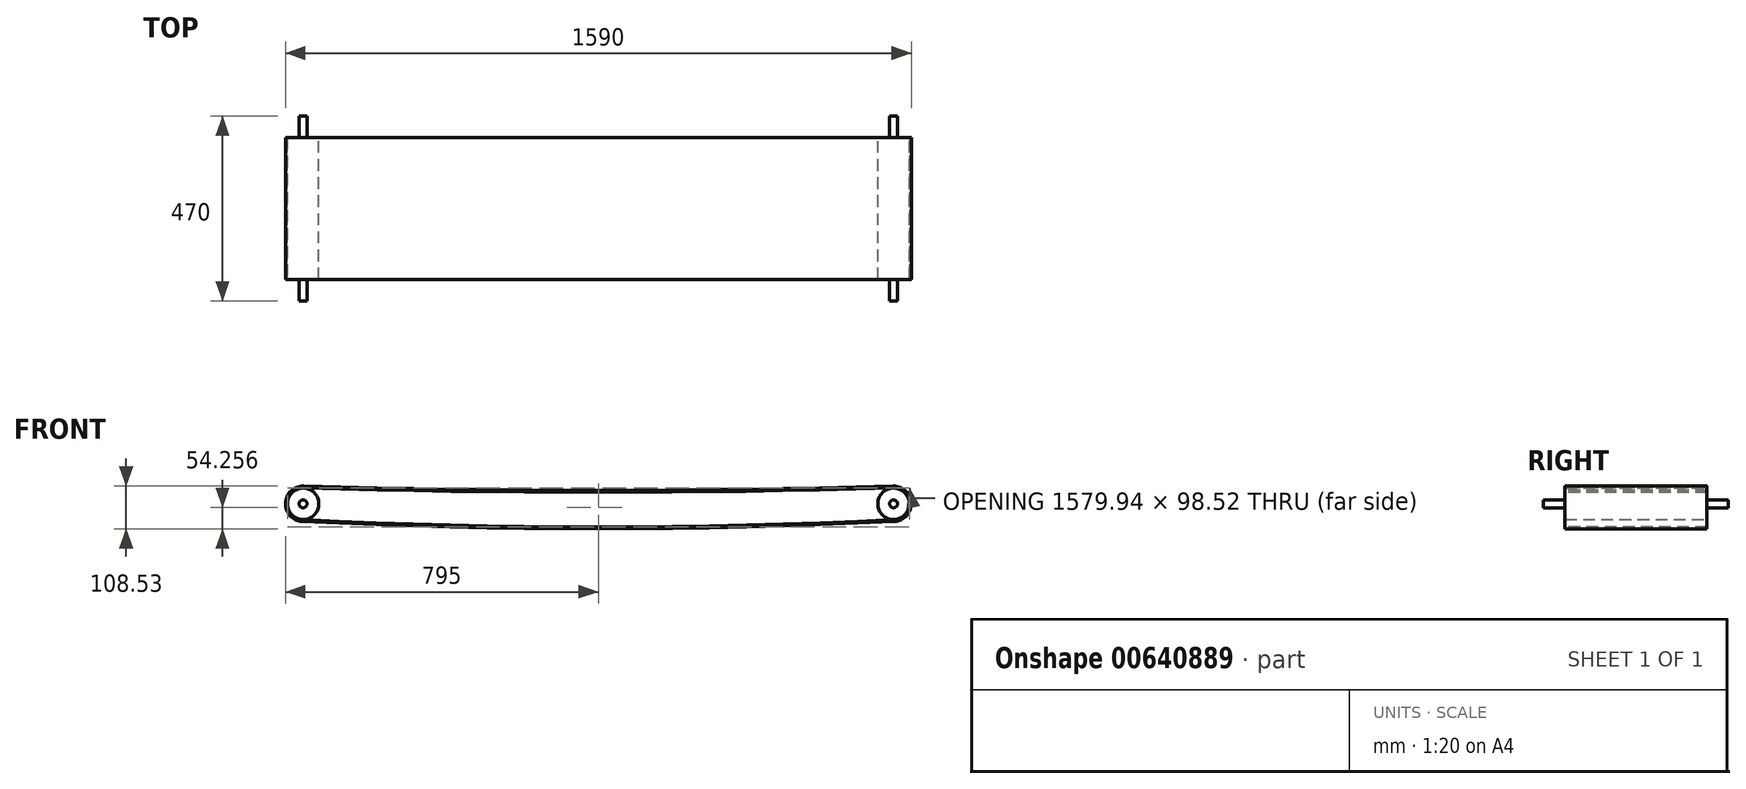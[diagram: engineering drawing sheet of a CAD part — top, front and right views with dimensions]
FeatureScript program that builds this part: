
annotation { "Feature Type Name" : "Feature", "Feature Type Description" : "" }
export const myFeature = defineFeature(function(context is Context, id is Id, definition is map)
    precondition{}
    {
        {
            var Q0;
            Q0=qCreatedBy(makeId("Front.planeOp"),FACE);
            var sketch = newSketch(context, id + "F0", { "sketchPlane" : qUnion([Q0])});
            skCircle(sketch, "E0", {"center": v(0, 0) * mm, "radius": 10 * mm});
            skSolve(sketch);
        }
        {
            var Q0;
            Q0 = qSketchRegion(id + "F0", true);
            extrude(context, id + "F1", {"entities" : qUnion([Q0]), "endBound" : BoundingType.SYMMETRIC, "depth" : 470 * mm, "offsetDistance" : 25.4 * mm});
        }
        {
            var Q0;
            Q0=qCreatedBy(makeId("Front.planeOp"),FACE);
            var sketch = newSketch(context, id + "F2", { "sketchPlane" : qUnion([Q0])});
            skCircle(sketch, "E1", {"center": v(0, 0) * mm, "radius": 40 * mm});
            skSolve(sketch);
        }
        {
            var Q0;
            Q0 = qSketchRegion(id + "F2", true);
            extrude(context, id + "F3", {"entities" : qUnion([Q0]), "operationType" : NewBodyOperationType.ADD, "endBound" : BoundingType.SYMMETRIC, "depth" : 360 * mm, "offsetDistance" : 25.4 * mm});
        }
        {
            var Q0;
            Q0=qCreatedBy(makeId("Right.planeOp"),FACE);
            cPlane(context, id + "F4", {"entities" : qUnion([Q0]), "cplaneType" : CPlaneType.OFFSET, "offset" : 750 * mm, "width" : 152.4 * mm, "height" : 152.4 * mm});
        }
        {
            var Q0;
            Q0=makeQuery(id+"F1.opExtrude","SWEPT_BODY",BODY,{"disambiguationData":[OSD([sQuery(id+"F0.wireOp",EDGE,"E0")])]});
            var Q1;
            Q1=qCreatedBy(id+"F4.planeOp",FACE);
            mirror(context, id + "F5", {"entities" : qUnion([Q0]), "mirrorPlane" : qUnion([Q1])});
        }
        {
            var Q0;
            Q0=makeQuery(id+"F3.opExtrude","CAP_FACE",FACE,{"disambiguationData":[OSD([sQuery(id+"F2.wireOp",EDGE,"E1")])],"isStart":false});
            cPlane(context, id + "F6", {"entities" : qUnion([Q0]), "cplaneType" : CPlaneType.OFFSET, "offset" : 0 * mm, "width" : 152.4 * mm, "height" : 152.4 * mm});
        }
        {
            var Q0;
            Q0=qCreatedBy(id+"F6.planeOp",FACE);
            var sketch = newSketch(context, id + "F7", { "sketchPlane" : qUnion([Q0])});
            skArc(sketch, "E2", {"start": v(1.14, 39.98) * mm, "mid": v(750, 29.33) * mm, "end": v(1498.86, 39.98) * mm});
            skArc(sketch, "E3", {"start": v(-1.98, -39.95) * mm, "mid": v(750, -58.53) * mm, "end": v(1501.98, -39.95) * mm});
            skArc(sketch, "E4", {"start": v(1.14, 39.98) * mm, "mid": v(-39.97, 1.56) * mm, "end": v(-1.98, -39.95) * mm});
            skArc(sketch, "E5", {"start": v(1501.98, -39.95) * mm, "mid": v(1539.97, 1.56) * mm, "end": v(1498.86, 39.98) * mm});
            skArc(sketch, "E6.0", {"start": v(1.28, 44.98) * mm, "mid": v(750, 34.33) * mm, "end": v(1498.72, 44.98) * mm});
            skArc(sketch, "E7.0", {"start": v(1.28, 44.98) * mm, "mid": v(-44.97, 1.75) * mm, "end": v(-2.22, -44.95) * mm});
            skArc(sketch, "E8.0", {"start": v(-2.22, -44.95) * mm, "mid": v(750, -63.53) * mm, "end": v(1502.22, -44.95) * mm});
            skArc(sketch, "E9.0", {"start": v(1502.22, -44.95) * mm, "mid": v(1544.97, 1.75) * mm, "end": v(1498.72, 44.98) * mm});
            skSolve(sketch);
        }
        {
            var Q0;
            Q0 = qSketchRegion(id + "F7", true);
            extrude(context, id + "F8", {"entities" : qUnion([Q0]), "oppositeDirection" : true, "depth" : 360.68 * mm, "offsetDistance" : 25.4 * mm});
        }
    });
